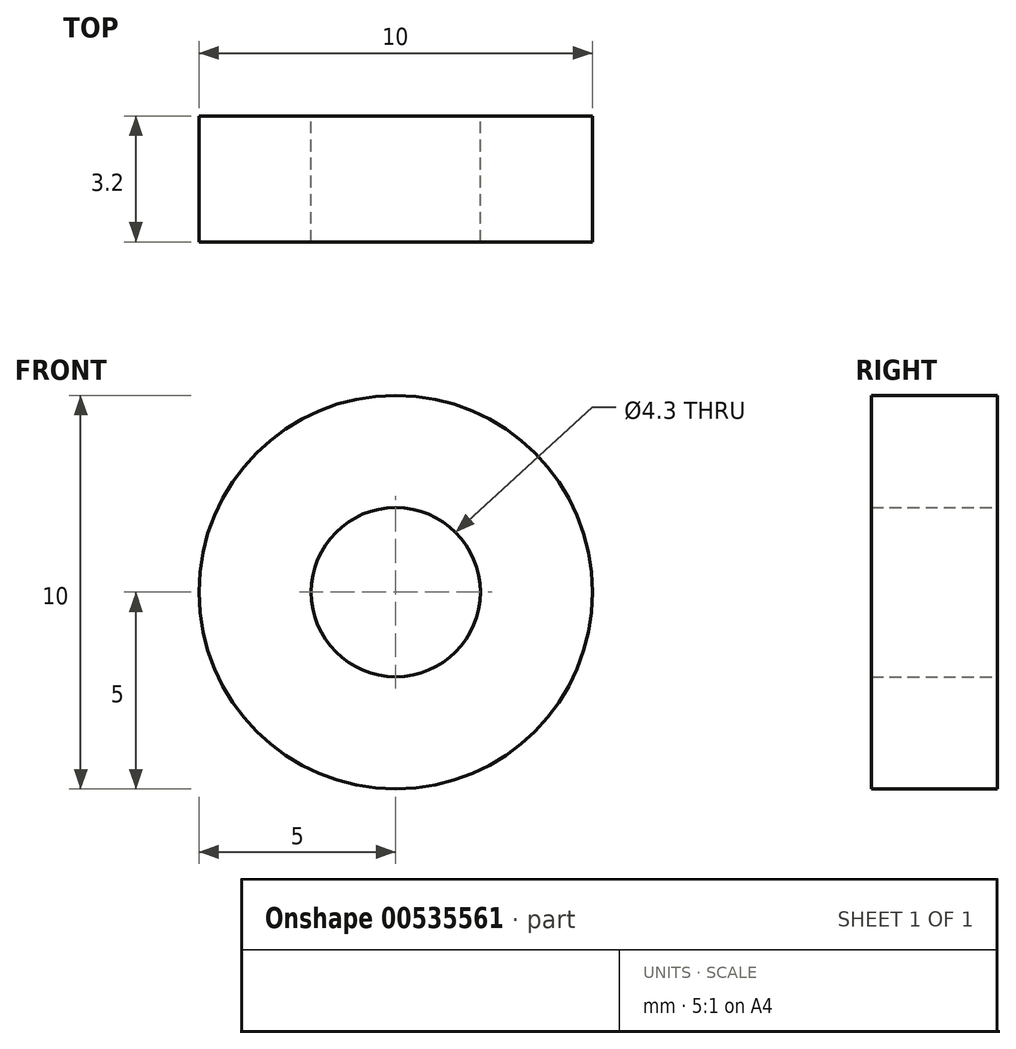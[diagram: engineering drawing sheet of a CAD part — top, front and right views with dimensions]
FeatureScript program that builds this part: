
annotation { "Feature Type Name" : "Feature", "Feature Type Description" : "" }
export const myFeature = defineFeature(function(context is Context, id is Id, definition is map)
    precondition{}
    {
        {
            var Q0;
            Q0=qCreatedBy(makeId("Front.planeOp"),FACE);
            var sketch = newSketch(context, id + "F0", { "sketchPlane" : qUnion([Q0])});
            skCircle(sketch, "E0", {"center": v(0, 0) * mm, "radius": 2.15 * mm});
            skCircle(sketch, "E1", {"center": v(0, 0) * mm, "radius": 5 * mm});
            skSolve(sketch);
        }
        {
            var Q0;
            Q0 = qSketchRegion(id + "F0", true);
            extrude(context, id + "F1", {"entities" : qUnion([Q0]), "depth" : 3.2 * mm, "offsetDistance" : 25 * mm});
        }
    });
